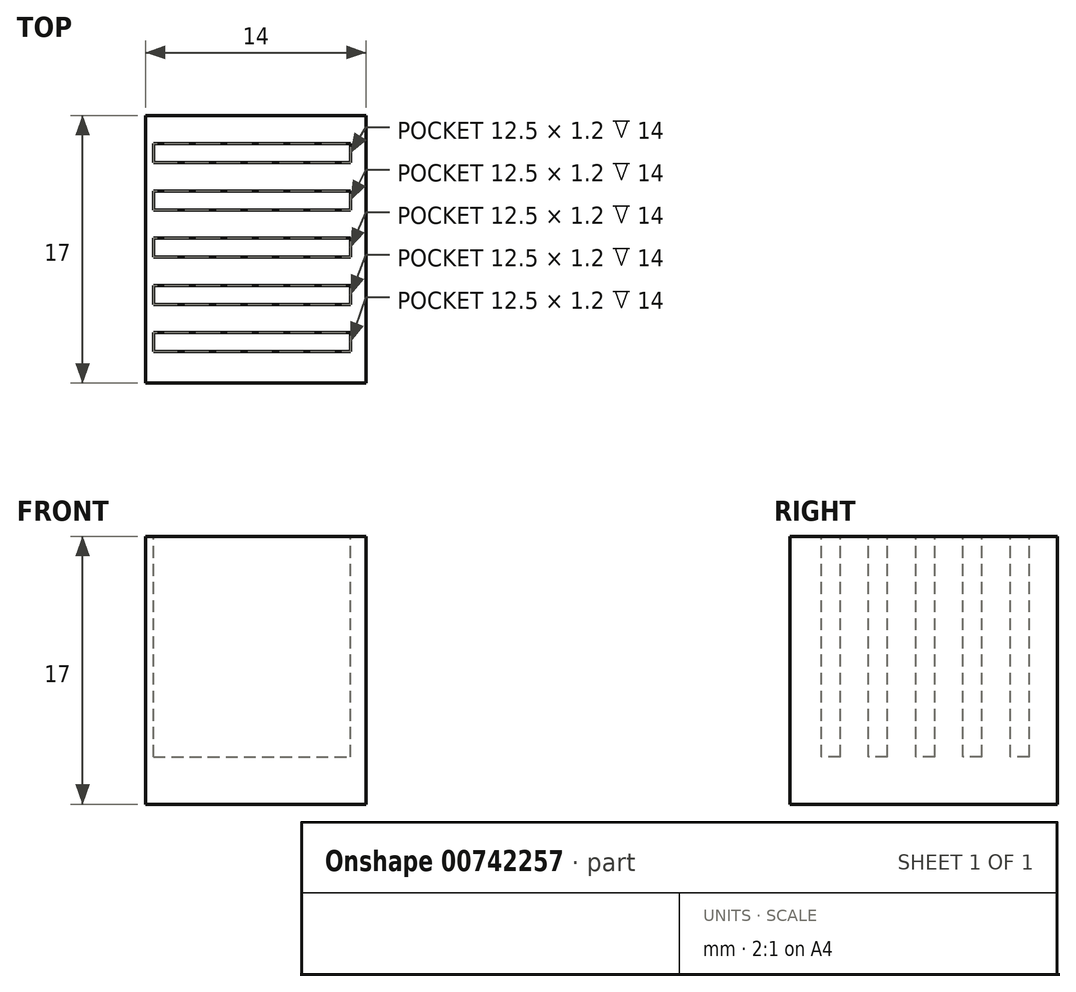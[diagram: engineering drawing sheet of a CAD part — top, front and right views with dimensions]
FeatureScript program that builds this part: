
annotation { "Feature Type Name" : "Feature", "Feature Type Description" : "" }
export const myFeature = defineFeature(function(context is Context, id is Id, definition is map)
    precondition{}
    {
        {
            var Q0;
            Q0=qCreatedBy(makeId("Front.planeOp"),FACE);
            var sketch = newSketch(context, id + "F0", { "sketchPlane" : qUnion([Q0])});
            skLineSegment(sketch, "E0.bottom", {"start": v(0, 0) * mm, "end": v(14, 0) * mm});
            skLineSegment(sketch, "E0.top", {"start": v(0, 17) * mm, "end": v(14, 17) * mm});
            skLineSegment(sketch, "E0.left", {"start": v(0, 0) * mm, "end": v(0, 17) * mm});
            skLineSegment(sketch, "E0.right", {"start": v(14, 0) * mm, "end": v(14, 17) * mm});
            skSolve(sketch);
        }
        {
            var Q0;
            Q0 = qSketchRegion(id + "F0", true);
            extrude(context, id + "F1", {"entities" : qUnion([Q0]), "oppositeDirection" : true, "depth" : 17 * mm, "offsetDistance" : 25 * mm});
        }
        {
            var Q0;
            Q0=makeQuery(id+"F1.opExtrude","SWEPT_FACE",FACE,{"disambiguationData":[OSD([sQuery(id+"F0.wireOp",EDGE,"E0.top")])]});
            var sketch = newSketch(context, id + "F2", { "sketchPlane" : qUnion([Q0])});
            skLineSegment(sketch, "E1.bottom", {"start": v(0.5, 3.2) * mm, "end": v(13, 3.2) * mm});
            skLineSegment(sketch, "E1.top", {"start": v(0.5, 2) * mm, "end": v(13, 2) * mm});
            skLineSegment(sketch, "E1.left", {"start": v(0.5, 3.2) * mm, "end": v(0.5, 2) * mm});
            skLineSegment(sketch, "E1.right", {"start": v(13, 3.2) * mm, "end": v(13, 2) * mm});
            skLineSegment(sketch, "E2.bottom", {"start": v(0.5, 6.2) * mm, "end": v(13, 6.2) * mm});
            skLineSegment(sketch, "E2.top", {"start": v(0.5, 5) * mm, "end": v(13, 5) * mm});
            skLineSegment(sketch, "E2.left", {"start": v(0.5, 6.2) * mm, "end": v(0.5, 5) * mm});
            skLineSegment(sketch, "E2.right", {"start": v(13, 6.2) * mm, "end": v(13, 5) * mm});
            skLineSegment(sketch, "E3.bottom", {"start": v(0.5, 9.2) * mm, "end": v(13, 9.2) * mm});
            skLineSegment(sketch, "E3.top", {"start": v(0.5, 8) * mm, "end": v(13, 8) * mm});
            skLineSegment(sketch, "E3.left", {"start": v(0.5, 9.2) * mm, "end": v(0.5, 8) * mm});
            skLineSegment(sketch, "E3.right", {"start": v(13, 9.2) * mm, "end": v(13, 8) * mm});
            skLineSegment(sketch, "E4.bottom", {"start": v(0.5, 12.2) * mm, "end": v(13, 12.2) * mm});
            skLineSegment(sketch, "E4.top", {"start": v(0.5, 11) * mm, "end": v(13, 11) * mm});
            skLineSegment(sketch, "E4.left", {"start": v(0.5, 12.2) * mm, "end": v(0.5, 11) * mm});
            skLineSegment(sketch, "E4.right", {"start": v(13, 12.2) * mm, "end": v(13, 11) * mm});
            skLineSegment(sketch, "E5.bottom", {"start": v(0.5, 15.2) * mm, "end": v(13, 15.2) * mm});
            skLineSegment(sketch, "E5.top", {"start": v(0.5, 14) * mm, "end": v(13, 14) * mm});
            skLineSegment(sketch, "E5.left", {"start": v(0.5, 15.2) * mm, "end": v(0.5, 14) * mm});
            skLineSegment(sketch, "E5.right", {"start": v(13, 15.2) * mm, "end": v(13, 14) * mm});
            skSolve(sketch);
        }
        {
            var Q0;
            Q0 = qSketchRegion(id + "F2", true);
            extrude(context, id + "F3", {"entities" : qUnion([Q0]), "operationType" : NewBodyOperationType.REMOVE, "oppositeDirection" : true, "depth" : 14 * mm, "offsetDistance" : 25 * mm});
        }
    });
